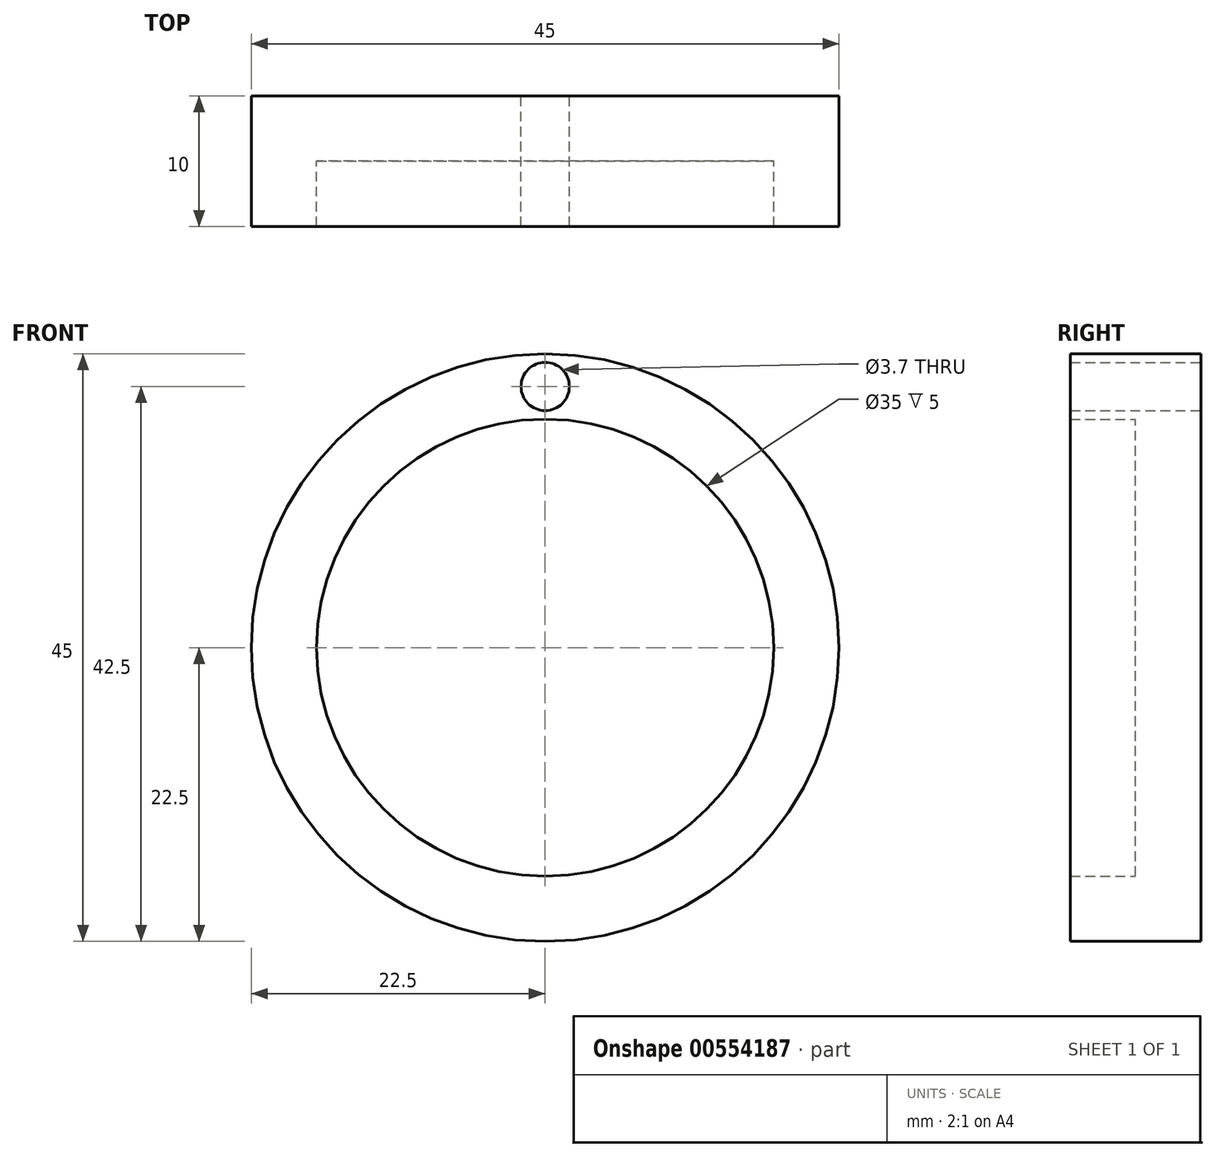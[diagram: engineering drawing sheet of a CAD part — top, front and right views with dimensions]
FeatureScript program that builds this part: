
annotation { "Feature Type Name" : "Feature", "Feature Type Description" : "" }
export const myFeature = defineFeature(function(context is Context, id is Id, definition is map)
    precondition{}
    {
        {
            var Q0;
            Q0=qCreatedBy(makeId("Front.planeOp"),FACE);
            var sketch = newSketch(context, id + "F0", { "sketchPlane" : qUnion([Q0])});
            skCircle(sketch, "E0", {"center": v(0, 0) * mm, "radius": 22.5 * mm});
            skCircle(sketch, "E1", {"center": v(0, 0) * mm, "radius": 17.5 * mm});
            skLineSegment(sketch, "E2", {"start": v(0, 22.5) * mm, "end": v(0, 17.5) * mm});
            skCircle(sketch, "E3", {"center": v(0, 20) * mm, "radius": 1.85 * mm});
            skSolve(sketch);
        }
        {
            var Q0;
            Q0=makeQuery(id+"F0.imprint","IMPRINT",FACE,{"disambiguationData":[TD([[makeQuery(id+"F0.imprint","IMPRINT",EDGE,{"derivedFrom":sQuery(id+"F0.wireOp",EDGE,"E1")}),1.0]])]});
            extrude(context, id + "F1", {"entities" : qUnion([Q0]), "depth" : 5 * mm, "offsetDistance" : 25 * mm});
        }
        {
            var Q0;
            Q0=makeQuery(id+"F0.imprint","IMPRINT",FACE,{"disambiguationData":[TD([[makeQuery(id+"F0.imprint","IMPRINT",EDGE,{"derivedFrom":sQuery(id+"F0.wireOp",EDGE,"E0")}),1.0]])]});
            extrude(context, id + "F2", {"entities" : qUnion([Q0]), "operationType" : NewBodyOperationType.ADD, "depth" : 10 * mm, "offsetDistance" : 25 * mm});
        }
    });
